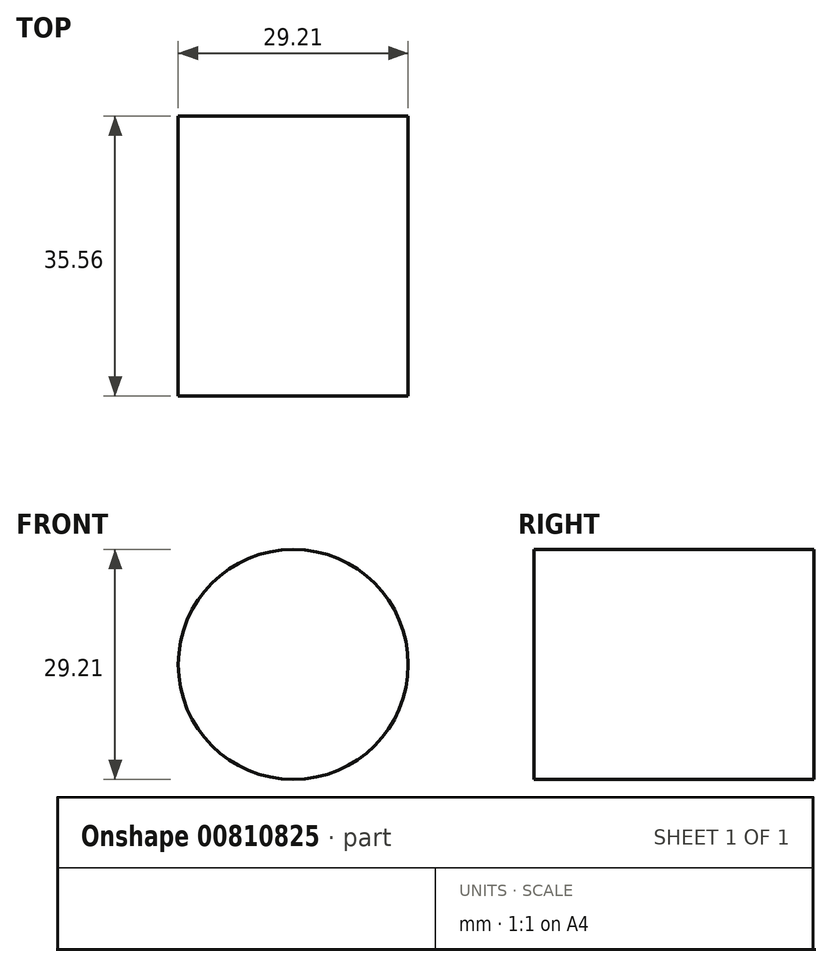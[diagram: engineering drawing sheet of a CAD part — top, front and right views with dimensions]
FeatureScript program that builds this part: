
annotation { "Feature Type Name" : "Feature", "Feature Type Description" : "" }
export const myFeature = defineFeature(function(context is Context, id is Id, definition is map)
    precondition{}
    {
        {
            var Q0;
            Q0=qCreatedBy(makeId("Front.planeOp"),FACE);
            var sketch = newSketch(context, id + "F0", { "sketchPlane" : qUnion([Q0])});
            skCircle(sketch, "E0", {"center": v(-19.3, 14.98) * mm, "radius": 14.6 * mm});
            skCircle(sketch, "E1", {"center": v(-19.3, 14.98) * mm, "radius": 1.02 * mm});
            skSolve(sketch);
        }
        {
            var Q0;
            Q0=makeQuery(id+"F0.imprint","IMPRINT",FACE,{"disambiguationData":[TD([[makeQuery(id+"F0.imprint","IMPRINT",EDGE,{"derivedFrom":sQuery(id+"F0.wireOp",EDGE,"E1")}),1.0]])]});
            var Q1;
            Q1=makeQuery(id+"F0.imprint","IMPRINT",FACE,{"disambiguationData":[TD([[makeQuery(id+"F0.imprint","IMPRINT",EDGE,{"derivedFrom":sQuery(id+"F0.wireOp",EDGE,"E0")}),1.0]])]});
            extrude(context, id + "F1", {"entities" : qUnion([Q0, Q1]), "depth" : 35.56 * mm, "offsetDistance" : 25.4 * mm});
        }
        {
            var Q0;
            Q0=sQuery(id+"F0.wireOp",EDGE,"E1");
            extrude(context, id + "F2", {"bodyType" : ToolBodyType.SURFACE, "surfaceEntities" : qUnion([Q0]), "depth" : 45.72 * mm, "offsetDistance" : 25.4 * mm});
        }
    });
